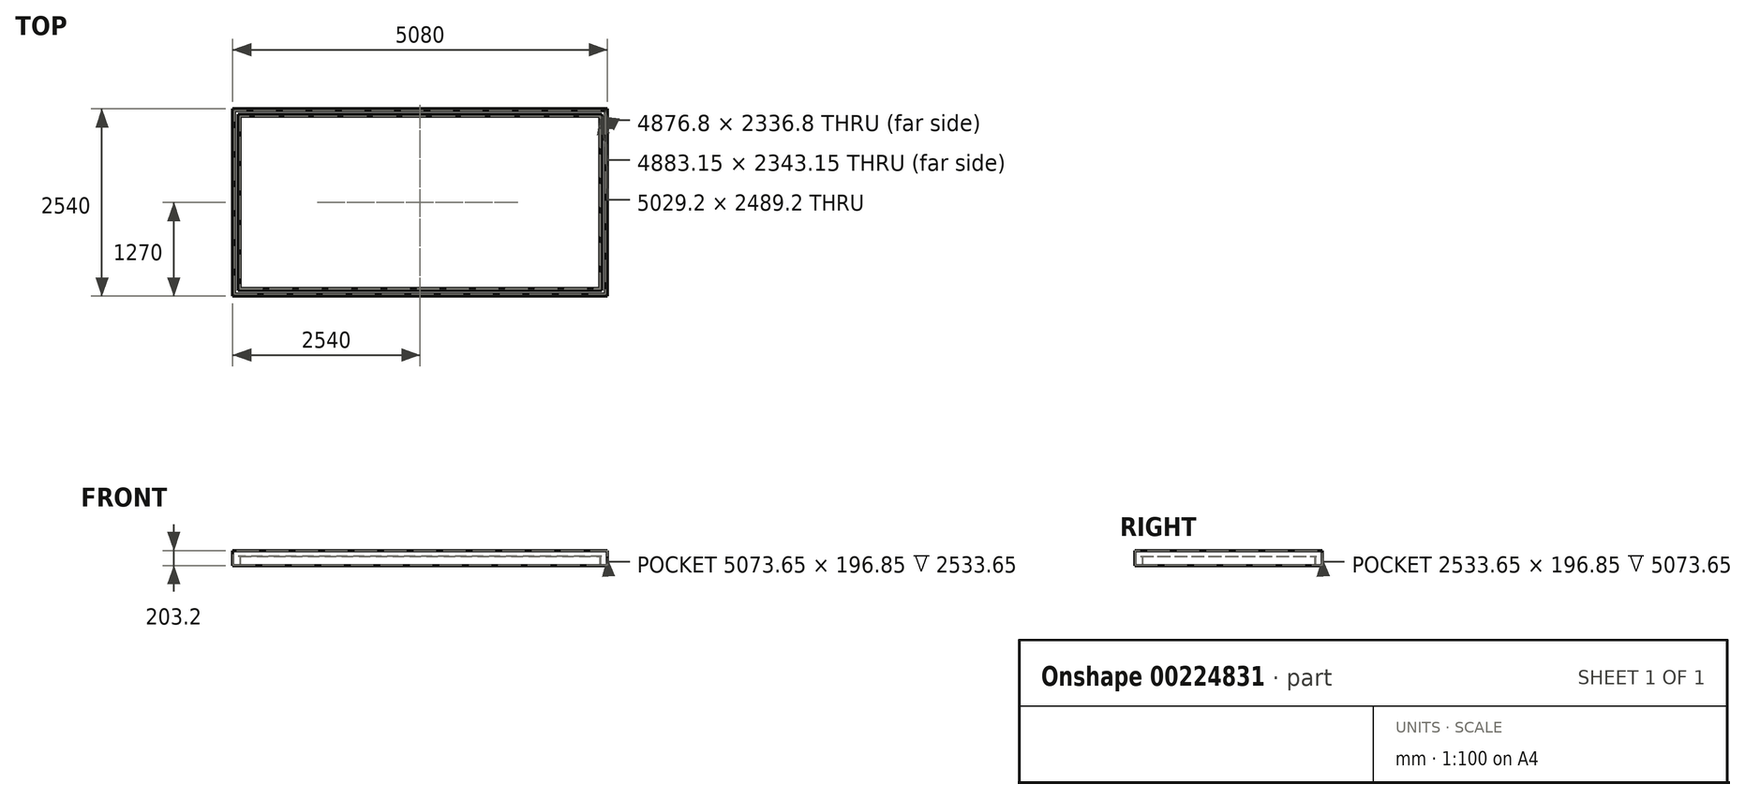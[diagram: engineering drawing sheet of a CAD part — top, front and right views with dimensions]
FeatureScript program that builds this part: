
annotation { "Feature Type Name" : "Feature", "Feature Type Description" : "" }
export const myFeature = defineFeature(function(context is Context, id is Id, definition is map)
    precondition{}
    {
        {
            var Q0;
            Q0=qCreatedBy(makeId("Top.planeOp"),FACE);
            var sketch = newSketch(context, id + "F0", { "sketchPlane" : qUnion([Q0])});
            skLineSegment(sketch, "E0.bottom", {"start": v(0, 0) * mm, "end": v(5080, 0) * mm});
            skLineSegment(sketch, "E0.top", {"start": v(0, 2540) * mm, "end": v(5080, 2540) * mm});
            skLineSegment(sketch, "E0.left", {"start": v(0, 0) * mm, "end": v(0, 2540) * mm});
            skLineSegment(sketch, "E0.right", {"start": v(5080, 0) * mm, "end": v(5080, 2540) * mm});
            skLineSegment(sketch, "E1.bottom", {"start": v(3.17, 3.18) * mm, "end": v(5076.83, 3.18) * mm});
            skLineSegment(sketch, "E1.top", {"start": v(3.17, 2536.82) * mm, "end": v(5076.83, 2536.82) * mm});
            skLineSegment(sketch, "E1.left", {"start": v(3.18, 3.17) * mm, "end": v(3.17, 2536.82) * mm});
            skLineSegment(sketch, "E1.right", {"start": v(5076.83, 3.17) * mm, "end": v(5076.83, 2536.82) * mm});
            skLineSegment(sketch, "E2.bottom", {"start": v(98.42, 98.43) * mm, "end": v(4981.57, 98.43) * mm});
            skLineSegment(sketch, "E2.top", {"start": v(98.42, 2441.57) * mm, "end": v(4981.57, 2441.57) * mm});
            skLineSegment(sketch, "E2.left", {"start": v(98.42, 98.43) * mm, "end": v(98.42, 2441.57) * mm});
            skLineSegment(sketch, "E2.right", {"start": v(4981.57, 98.43) * mm, "end": v(4981.57, 2441.57) * mm});
            skLineSegment(sketch, "E3.bottom", {"start": v(101.6, 101.6) * mm, "end": v(4978.4, 101.6) * mm});
            skLineSegment(sketch, "E3.top", {"start": v(101.6, 2438.4) * mm, "end": v(4978.4, 2438.4) * mm});
            skLineSegment(sketch, "E3.left", {"start": v(101.6, 101.6) * mm, "end": v(101.6, 2438.4) * mm});
            skLineSegment(sketch, "E3.right", {"start": v(4978.4, 101.6) * mm, "end": v(4978.4, 2438.4) * mm});
            skSolve(sketch);
        }
        {
            var Q0;
            Q0=makeQuery(id+"F0.imprint","IMPRINT",FACE,{"disambiguationData":[TD([[makeQuery(id+"F0.imprint","IMPRINT",EDGE,{"derivedFrom":sQuery(id+"F0.wireOp",EDGE,"E0.bottom")}),1.0]])]});
            extrude(context, id + "F1", {"entities" : qUnion([Q0]), "depth" : 200.02 * mm});
        }
        {
            var Q0;
            Q0=makeQuery(id+"F0.imprint","IMPRINT",FACE,{"disambiguationData":[TD([[makeQuery(id+"F0.imprint","IMPRINT",EDGE,{"derivedFrom":sQuery(id+"F0.wireOp",EDGE,"E2.bottom")}),1.0]])]});
            extrude(context, id + "F2", {"entities" : qUnion([Q0]), "operationType" : NewBodyOperationType.ADD, "depth" : 123.82 * mm});
        }
        {
            var Q0;
            Q0=makeQuery(id+"F0.imprint","IMPRINT",FACE,{"disambiguationData":[TD([[makeQuery(id+"F0.imprint","IMPRINT",EDGE,{"derivedFrom":sQuery(id+"F0.wireOp",EDGE,"E1.bottom")}),1.0]])]});
            extrude(context, id + "F3", {"entities" : qUnion([Q0]), "operationType" : NewBodyOperationType.ADD, "depth" : 3.17 * mm});
        }
        {
            var Q0;
            Q0=makeQuery(id+"F2.opExtrude","CAP_FACE",FACE,{"disambiguationData":[OSD([sQuery(id+"F0.wireOp",EDGE,"E2.bottom"),sQuery(id+"F0.wireOp",EDGE,"E2.top"),sQuery(id+"F0.wireOp",EDGE,"E2.left"),sQuery(id+"F0.wireOp",EDGE,"E2.right"),sQuery(id+"F0.wireOp",EDGE,"E3.bottom"),sQuery(id+"F0.wireOp",EDGE,"E3.top"),sQuery(id+"F0.wireOp",EDGE,"E3.left"),sQuery(id+"F0.wireOp",EDGE,"E3.right")])],"isStart":false});
            var sketch = newSketch(context, id + "F4", { "sketchPlane" : qUnion([Q0])});
            skLineSegment(sketch, "E4.bottom", {"start": v(101.6, 2438.4) * mm, "end": v(4978.4, 2438.4) * mm});
            skLineSegment(sketch, "E4.top", {"start": v(101.6, 101.6) * mm, "end": v(4978.4, 101.6) * mm});
            skLineSegment(sketch, "E4.left", {"start": v(101.6, 2438.4) * mm, "end": v(101.6, 101.6) * mm});
            skLineSegment(sketch, "E4.right", {"start": v(4978.4, 2438.4) * mm, "end": v(4978.4, 101.6) * mm});
            skLineSegment(sketch, "E5.bottom", {"start": v(5003.8, 76.2) * mm, "end": v(76.2, 76.2) * mm});
            skLineSegment(sketch, "E5.top", {"start": v(5003.8, 2463.8) * mm, "end": v(76.2, 2463.8) * mm});
            skLineSegment(sketch, "E5.left", {"start": v(5003.8, 76.2) * mm, "end": v(5003.8, 2463.8) * mm});
            skLineSegment(sketch, "E5.right", {"start": v(76.2, 76.2) * mm, "end": v(76.2, 2463.8) * mm});
            skSolve(sketch);
        }
        {
            var Q0;
            Q0 = qSketchRegion(id + "F4", true);
            extrude(context, id + "F5", {"entities" : qUnion([Q0]), "operationType" : NewBodyOperationType.ADD, "depth" : 3.17 * mm});
        }
        {
            var Q0;
            Q0=makeQuery(id+"F1.opExtrude","CAP_FACE",FACE,{"disambiguationData":[OSD([sQuery(id+"F0.wireOp",EDGE,"E0.bottom"),sQuery(id+"F0.wireOp",EDGE,"E0.top"),sQuery(id+"F0.wireOp",EDGE,"E0.left"),sQuery(id+"F0.wireOp",EDGE,"E0.right"),sQuery(id+"F0.wireOp",EDGE,"E1.bottom"),sQuery(id+"F0.wireOp",EDGE,"E1.top"),sQuery(id+"F0.wireOp",EDGE,"E1.left"),sQuery(id+"F0.wireOp",EDGE,"E1.right")])],"isStart":false});
            var sketch = newSketch(context, id + "F6", { "sketchPlane" : qUnion([Q0])});
            skLineSegment(sketch, "E6.bottom", {"start": v(0, 0) * mm, "end": v(5080, 0) * mm});
            skLineSegment(sketch, "E6.top", {"start": v(0, 2540) * mm, "end": v(5080, 2540) * mm});
            skLineSegment(sketch, "E6.left", {"start": v(0, 0) * mm, "end": v(0, 2540) * mm});
            skLineSegment(sketch, "E6.right", {"start": v(5080, 0) * mm, "end": v(5080, 2540) * mm});
            skLineSegment(sketch, "E7.bottom", {"start": v(5054.6, 2514.6) * mm, "end": v(25.4, 2514.6) * mm});
            skLineSegment(sketch, "E7.top", {"start": v(5054.6, 25.4) * mm, "end": v(25.4, 25.4) * mm});
            skLineSegment(sketch, "E7.left", {"start": v(5054.6, 2514.6) * mm, "end": v(5054.6, 25.4) * mm});
            skLineSegment(sketch, "E7.right", {"start": v(25.4, 2514.6) * mm, "end": v(25.4, 25.4) * mm});
            skSolve(sketch);
        }
        {
            var Q0;
            Q0 = qSketchRegion(id + "F6", true);
            extrude(context, id + "F7", {"entities" : qUnion([Q0]), "operationType" : NewBodyOperationType.ADD, "depth" : 3.17 * mm});
        }
    });
